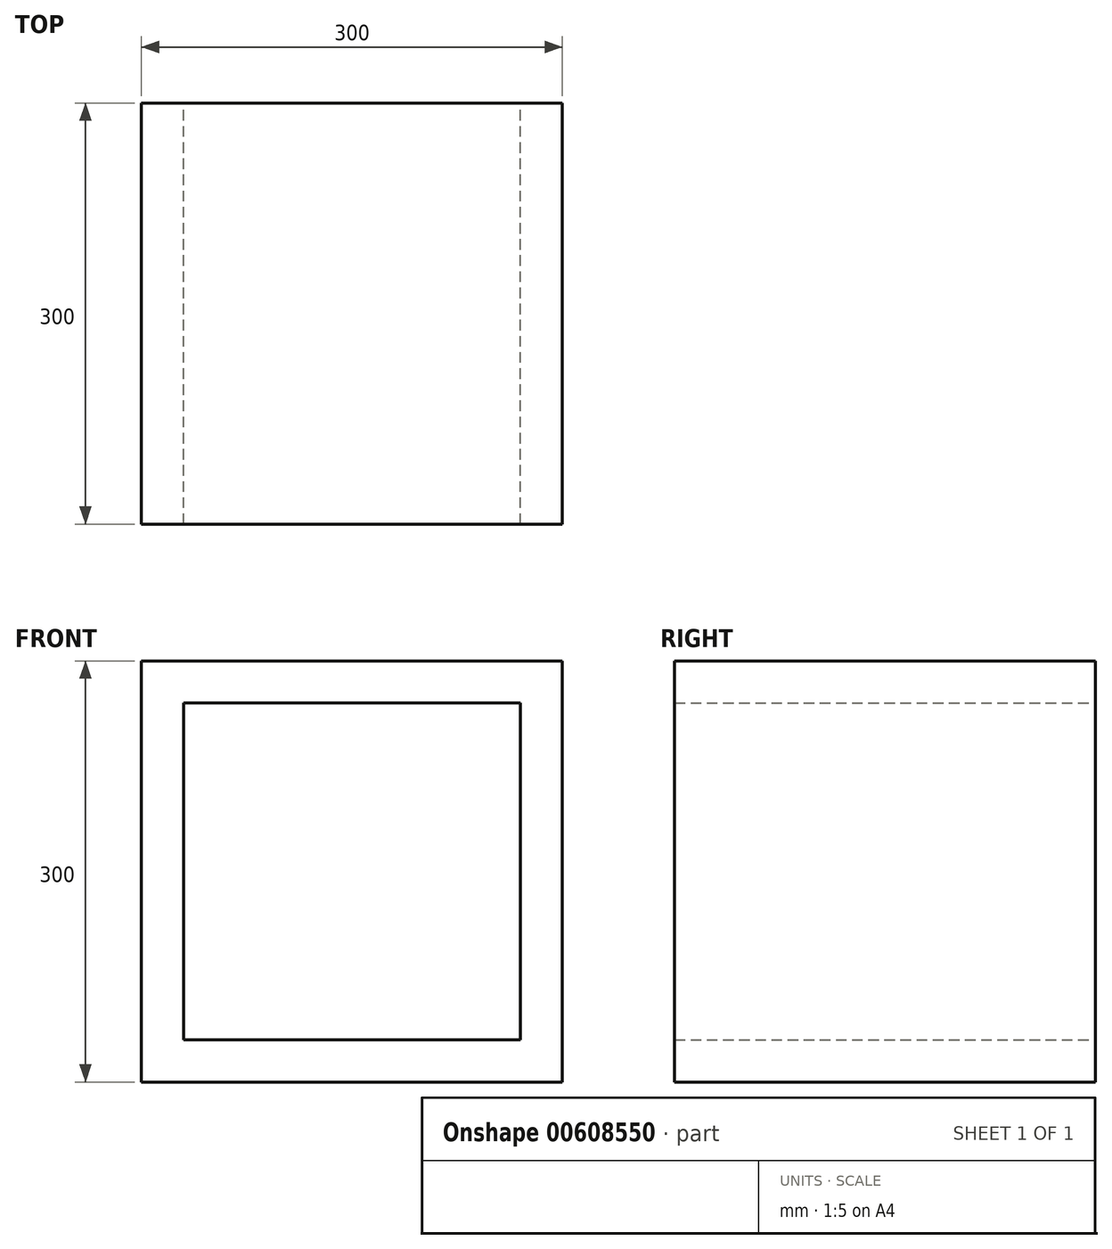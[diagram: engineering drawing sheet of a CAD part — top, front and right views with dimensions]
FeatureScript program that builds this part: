
annotation { "Feature Type Name" : "Feature", "Feature Type Description" : "" }
export const myFeature = defineFeature(function(context is Context, id is Id, definition is map)
    precondition{}
    {
        {
            assignVariable(context, id + "F0", {"name" : "depth", "anyValue" : 300});
        }
        {
            var Q0;
            Q0=qCreatedBy(makeId("Front.planeOp"),FACE);
            var sketch = newSketch(context, id + "F1", { "sketchPlane" : qUnion([Q0])});
            skLineSegment(sketch, "E0.bottom", {"start": v(150, -150) * mm, "end": v(-150, -150) * mm});
            skLineSegment(sketch, "E0.top", {"start": v(150, 150) * mm, "end": v(-150, 150) * mm});
            skLineSegment(sketch, "E0.left", {"start": v(150, -150) * mm, "end": v(150, 150) * mm});
            skLineSegment(sketch, "E0.right", {"start": v(-150, -150) * mm, "end": v(-150, 150) * mm});
            skPoint(sketch, "E0.middle", {"position": v(0, 0) * mm});
            skLineSegment(sketch, "E1.0", {"start": v(120, -120) * mm, "end": v(120, 120) * mm});
            skLineSegment(sketch, "E1.1", {"start": v(120, -120) * mm, "end": v(-120, -120) * mm});
            skLineSegment(sketch, "E1.2", {"start": v(-120, -120) * mm, "end": v(-120, 120) * mm});
            skLineSegment(sketch, "E1.3", {"start": v(120, 120) * mm, "end": v(-120, 120) * mm});
            skSolve(sketch);
        }
        {
            var Q0;
            Q0=makeQuery(id+"F1.imprint","IMPRINT",FACE,{"disambiguationData":[TD([[makeQuery(id+"F1.imprint","IMPRINT",EDGE,{"derivedFrom":sQuery(id+"F1.wireOp",EDGE,"E0.bottom")}),-1.0]])]});
            extrude(context, id + "F2", {"entities" : qUnion([Q0]), "depth" : getVariable(context, 'depth') * mm, "offsetDistance" : 25 * mm});
        }
    });
